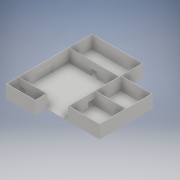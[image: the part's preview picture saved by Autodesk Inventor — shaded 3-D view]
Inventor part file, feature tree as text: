
AUTODESK INVENTOR PART (.ipt)
format: ipt  version: 2017 (Build 210142000, 142)  size: 746,496 bytes
history: native  units: in
note: dims shown in document units (in); Inventor stores cm internally (conversion verified against a paired STEP export)
features: sketch x48, extrude x47, fillet x2, helix x1, other x1
ambient origin geometry x8: Origin, YZ Plane, XZ Plane, XY Plane, X Axis, Y Axis, Z Axis, Center Point
bodies: Solid1 (feature_tree)
feature tree (99):
  extrude  "Door Frame CR"  Depth=7.5in
  extrude  "Door Frame left Extruded"  Depth=11.0in
  extrude  "Door Frame right Extruded"  Depth=0.35in TaperAngle=0.0deg
  extrude  "Floor"  Depth=27.0in TaperAngle=0.0deg
  extrude  "Walls"  Depth=30.0in TaperAngle=0.0deg
  extrude  "Door Fram ex"  Depth=0.3in TaperAngle=0.0deg
  fillet  "Dorr Fillet"  Radius=0.3in
  fillet  "Door Fillet"  Radius=0.3in
  extrude  "Door floor"  Depth=0.3125in TaperAngle=0.0deg
  extrude  "wall board middle"  Depth=0.02in
  extrude  "Wall board left"  Depth=0.35in
  extrude  "Wall board right"  Depth=1.455in
  extrude  "Wall board door"  Depth=1.4574in
  extrude  "Door mid"  Depth=0.1in TaperAngle=0.0deg
  extrude  "Main wall left"  Depth=0.1in TaperAngle=0.0deg
  extrude  "Main wall right"  Depth=65.5in
  extrude  "prob the floor"  Depth=65.5in
  extrude  "wall board front main 1"  TaperAngle=0.0deg  [1 undecoded]
  extrude  "wall board front main 2"  TaperAngle=0.0deg  [1 undecoded]
  extrude  "wall board front left"  Depth=0.1in TaperAngle=0.0deg
  extrude  "wall board front right"  Depth=0.1in TaperAngle=0.0deg
  extrude  "Right doors"  Depth=7.5in
  sketch  "Sketch33"  dims[d67=0.1in d68=0.0in d69=7.5in]
  extrude  "Right doors head"  Depth=7.5in
  sketch  "Sketch35"  dims[d72=11.0in d73=3.0in d74=0.05in d75=0.0in d76=0.0in]
  extrude  "Right doors frame mid"  Depth=0.05in TaperAngle=0.0deg
  extrude  "right doors frame into"  Depth=1.72in
  extrude  "Room 2 & 3 wall "  Depth=0.3049in
  extrude  "Room 3 wall right"  Depth=0.3in TaperAngle=0.0deg
  extrude  "Room 3 wall mid"  Depth=40.0in TaperAngle=0.0deg
  extrude  "Room 3 Floor"  Depth=40.0in TaperAngle=0.0deg
  extrude  "Room 2 mid wall"  Depth=10.8in
  extrude  "Room 2 wall left"  Depth=40.0in TaperAngle=0.0deg
  extrude  "Room 2 floor"  Depth=10.8in
  extrude  "Room 2 wall board left"  Depth=0.6in
  extrude  "Room 3 wall board left"  Depth=39.9in TaperAngle=0.0deg
  extrude  "Room 2 & 3 wall board mid"  Depth=1.255in
  extrude  "Room 2 wall board right"  Depth=1.255in
  extrude  "Room 3 wall board door"  Depth=1.255in
  extrude  "Room 2 wall board door"  Depth=1.255in
  extrude  "Fake Door Frame"  Depth=1.255in
  extrude  "My mistake ;-;"  Depth=0.1in TaperAngle=0.0deg
  extrude  "Closet main wall"  Depth=0.15in TaperAngle=0.0deg
  extrude  "Closet left and right wall"  Depth=37.0in TaperAngle=0.0deg
  extrude  "Closet back wall"  Depth=0.6in
  extrude  "Closet Floor"  Depth=0.6in
  extrude  "Closet Outter wall board"  Depth=15.0in TaperAngle=0.0deg
  extrude  "Closet Door Frame"  Depth=0.315in TaperAngle=0.0deg
  extrude  "Extrusion47"  Depth=0.6in
  extrude  "Mistakes were made"  Depth=6.0in TaperAngle=0.0deg
  extrude  "LETS RAISE THE... walls"  [1 undecoded]
  helix  "Coil1"  [1 undecoded]
  sketch  "Sketch1"  dims[d0=9.0in d1=7.5in]
  sketch  "Sketch2"  dims[d2=2.0in d3=11.0in]
  sketch  "Sketch4"  dims[d4=11.5in d5=0.35in d6=0.0in]
  sketch  "Sketch5"  dims[d7=27.0in d8=0.0in d9=27.0in d10=0.0in]
  sketch  "Sketch7"  dims[d11=0.2in d12=30.0in d13=0.0in]
  other  "Door Frame"
  sketch  "Sketch9"  dims[d21=0.5in d22=10.8125in d23=0.0in d27=0.3in d28=0.3in]
  sketch  "Sketch13"  dims[d29=0.3in d30=0.3125in d31=0.0in]
  sketch  "Sketch14"  dims[d32=0.02in d33=0.02in]
  sketch  "Sketch16"  dims[d34=0.35in d35=0.0in d36=1.3in]
  sketch  "Sketch20"  dims[d37=0.1in d38=0.0in d39=1.455in]
  sketch  "Sketch22"  dims[d40=0.1in d41=0.0in d42=1.4574in]
  sketch  "Sketch23"  dims[d43=1.457in d44=0.1in d45=0.0in]
  sketch  "Sketch24"  dims[d47=1.457in d49=0.1in d50=0.0in]
  sketch  "Sketch26"  dims[d51=0.35in d52=0.0in d53=65.5in]
  sketch  "Sketch27"  dims[d54=0.0in d55=65.5in]
  sketch  "Sketch28"  dims[d56=65.5in d57=0.0in]
  sketch  "Sketch30"  dims[d58=65.5in d59=0.0in]
  sketch  "Sketch31"  dims[d60=1.4574in d61=0.1in d62=0.0in]
  sketch  "Sketch32"  dims[d63=0.1in d64=0.0in d65=0.1in d66=0.0in]
  sketch  "Sketch34"  dims[d70=7.5in d71=11.0in]
  sketch  "Sketch36"  dims[d77=1.72in d78=1.72in]
  sketch  "Sketch38"  dims[d79=20.375in d80=0.0in d81=0.3049in]
  sketch  "Sketch41"  dims[d82=0.3049in d87=0.3in d88=0.0in]
  sketch  "Sketch45"  dims[d90=0.3in d91=0.0in d94=40.0in d95=0.0in]
  sketch  "Sketch47"  dims[d96=10.8in d99=40.0in d100=0.0in]
  sketch  "Sketch48"  dims[d101=0.6in d102=10.8in]
  sketch  "Sketch49"  dims[d103=33.5in d104=0.0in d105=40.0in d106=0.0in]
  sketch  "Sketch50"  dims[d107=0.6in d108=10.8in]
  sketch  "Sketch54"  dims[d109=33.5in d110=0.0in d111=0.6in]
  sketch  "Sketch55"  dims[d112=10.8in d113=39.9in d114=0.0in]
  sketch  "Sketch56"  dims[d115=40.0in d116=0.0in d117=1.255in]
  sketch  "Sketch58"  dims[d118=0.1in d119=0.0in d120=1.255in]
  sketch  "Sketch59"  dims[d121=0.1in d122=0.0in d123=1.255in]
  sketch  "Sketch60"  dims[d124=0.1in d125=0.0in d129=1.255in]
  sketch  "Sketch62"  dims[d130=0.1in d131=0.0in d132=1.255in]
  sketch  "Sketch64"  dims[d133=0.1in d134=0.0in d135=0.1in d136=0.0in]
  sketch  "Sketch67"  dims[d137=0.315in d138=0.0in d139=0.15in d140=0.0in]
  sketch  "Sketch68"  dims[d141=0.6in d142=37.0in d143=0.0in]
  sketch  "Sketch69"  dims[d144=0.6in d145=0.6in]
  sketch  "Sketch70"  dims[d146=15.0in d147=0.0in d148=0.6in]
  sketch  "Sketch73"  dims[d149=36.4375in d150=0.0in d151=15.0in d152=0.0in]
  sketch  "Sketch74"  dims[d153=0.15in d154=0.0in d160=0.315in d161=0.0in]
  sketch  "Sketch76"  dims[d162=3.0in d163=0.0in]
  sketch  "Sketch77"  dims[d164=96.0in d165=1.0in d166=0.5906in d167=0.0in d168=90.0deg d169=90.0deg d170=0.0in d171=0.0in d172=0.6in]
  sketch  "Sketch88"  dims[d176=116.625in d177=0.0in d178=6.0in d179=0.0in]
  sketch  "Sketch89"
note: 4 required parameter values undecoded (feature->parameter linkage not recoverable at this tier; creation-order binding heuristic only, values carry confidence <= 0.55)
